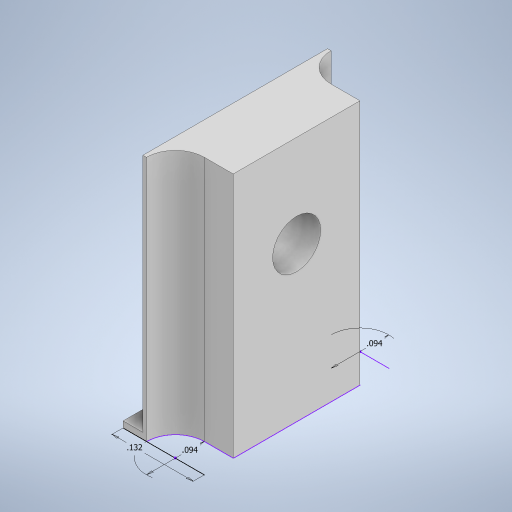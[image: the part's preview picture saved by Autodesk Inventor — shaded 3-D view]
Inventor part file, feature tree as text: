
AUTODESK INVENTOR PART (.ipt)
format: ipt  version: 2023 (Build 270158000, 158)  size: 238,592 bytes
history: native  units: in
note: dims shown in document units (in); Inventor stores cm internally (conversion verified against a paired STEP export)
features: extrude x3, sketch x2
ambient origin geometry x8: Origin, YZ Plane, XZ Plane, XY Plane, X Axis, Y Axis, Z Axis, Center Point
bodies: Solid1 (feature_tree)
feature tree (5):
  sketch  "Sketch1"  dims[d2=0.094in d3=0.094in]
  extrude  "Extrusion1"  Depth=0.094in
  extrude  "Extrusion3"  Depth=0.01in
  extrude  "Extrusion4"  Depth=0.01in
  sketch  "Sketch2"  dims[d4=0.4in d5=0.0in d8=0.0781in d9=0.25in d10=5.0in d11=0.0in d12=0.132in d13=0.01in d14=0.0in]
